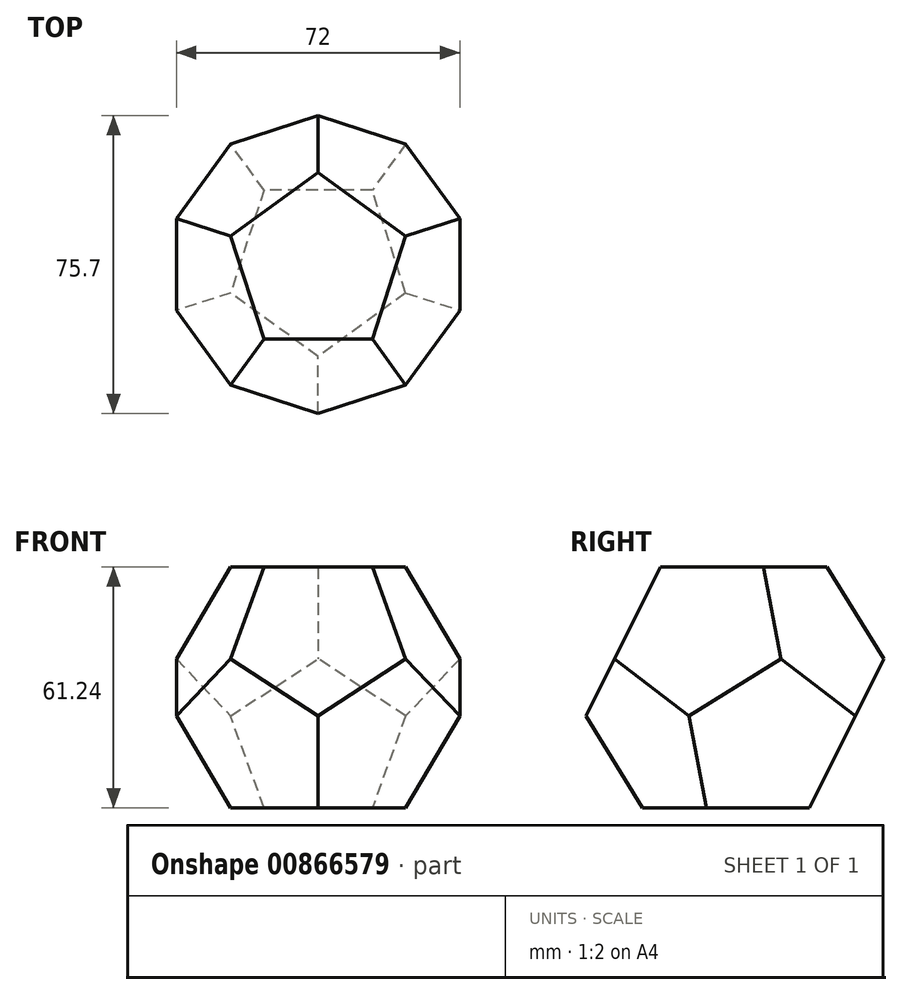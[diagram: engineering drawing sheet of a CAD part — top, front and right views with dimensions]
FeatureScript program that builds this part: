
annotation { "Feature Type Name" : "Feature", "Feature Type Description" : "" }
export const myFeature = defineFeature(function(context is Context, id is Id, definition is map)
    precondition{}
    {
        {
            var Q0;
            Q0=qCreatedBy(makeId("Top.planeOp"),FACE);
            var sketch = newSketch(context, id + "F0", { "sketchPlane" : qUnion([Q0])});
            skLineSegment(sketch, "E0.bottom", {"start": v(36, 36) * mm, "end": v(-36, 36) * mm, "construction": true});
            skLineSegment(sketch, "E0.top", {"start": v(36, -36) * mm, "end": v(-36, -36) * mm, "construction": true});
            skLineSegment(sketch, "E0.left", {"start": v(36, 36) * mm, "end": v(36, -36) * mm, "construction": true});
            skLineSegment(sketch, "E0.right", {"start": v(-36, 36) * mm, "end": v(-36, -36) * mm, "construction": true});
            skPoint(sketch, "E0.middle", {"position": v(0, 0) * mm});
            skCircle(sketch, "E1.cCircle", {"center": v(0, 0) * mm, "radius": 36 * mm, "construction": true});
            skLineSegment(sketch, "E1.0", {"start": v(-36, -11.7) * mm, "end": v(-36, 11.7) * mm});
            skLineSegment(sketch, "E1.1", {"start": v(-36, 11.7) * mm, "end": v(-22.25, 30.62) * mm});
            skLineSegment(sketch, "E1.2", {"start": v(-22.25, 30.62) * mm, "end": v(0, 37.85) * mm});
            skLineSegment(sketch, "E1.3", {"start": v(0, 37.85) * mm, "end": v(22.25, 30.62) * mm});
            skLineSegment(sketch, "E1.4", {"start": v(22.25, 30.62) * mm, "end": v(36, 11.7) * mm});
            skLineSegment(sketch, "E1.5", {"start": v(36, 11.7) * mm, "end": v(36, -11.7) * mm});
            skLineSegment(sketch, "E1.6", {"start": v(36, -11.7) * mm, "end": v(22.25, -30.62) * mm});
            skLineSegment(sketch, "E1.7", {"start": v(22.25, -30.62) * mm, "end": v(0, -37.85) * mm});
            skLineSegment(sketch, "E1.8", {"start": v(0, -37.85) * mm, "end": v(-22.25, -30.62) * mm});
            skLineSegment(sketch, "E1.9", {"start": v(-22.25, -30.62) * mm, "end": v(-36, -11.7) * mm});
            skPoint(sketch, "E1.0.midPoint", {"position": v(-36, 0) * mm});
            skSolve(sketch);
        }
        {
            var Q0;
            Q0 = qSketchRegion(id + "F0", true);
            extrude(context, id + "F1", {"entities" : qUnion([Q0]), "depth" : 61.25 * mm, "offsetDistance" : 25 * mm, "symmetric" : true});
        }
        {
            var Q0;
            Q0=makeQuery(id+"F1.opExtrude","CAP_FACE",FACE,{"disambiguationData":[OSD([sQuery(id+"F0.wireOp",EDGE,"E1.0"),sQuery(id+"F0.wireOp",EDGE,"E1.1"),sQuery(id+"F0.wireOp",EDGE,"E1.2"),sQuery(id+"F0.wireOp",EDGE,"E1.3"),sQuery(id+"F0.wireOp",EDGE,"E1.4"),sQuery(id+"F0.wireOp",EDGE,"E1.5"),sQuery(id+"F0.wireOp",EDGE,"E1.6"),sQuery(id+"F0.wireOp",EDGE,"E1.7"),sQuery(id+"F0.wireOp",EDGE,"E1.8"),sQuery(id+"F0.wireOp",EDGE,"E1.9")])],"isStart":false});
            var sketch = newSketch(context, id + "F2", { "sketchPlane" : qUnion([Q0])});
            skCircle(sketch, "E2.cCircle", {"center": v(0, 0) * mm, "radius": 23.4 * mm, "construction": true});
            skLineSegment(sketch, "E2.0", {"start": v(0, 23.4) * mm, "end": v(22.25, 7.23) * mm});
            skLineSegment(sketch, "E2.1", {"start": v(22.25, 7.23) * mm, "end": v(13.75, -18.93) * mm});
            skLineSegment(sketch, "E2.2", {"start": v(13.75, -18.93) * mm, "end": v(-13.75, -18.93) * mm});
            skLineSegment(sketch, "E2.3", {"start": v(-13.75, -18.93) * mm, "end": v(-22.25, 7.23) * mm});
            skLineSegment(sketch, "E2.4", {"start": v(-22.25, 7.23) * mm, "end": v(0, 23.4) * mm});
            skSolve(sketch);
        }
        {
            var Q0;
            Q0=qCreatedBy(makeId("Right.planeOp"),FACE);
            var sketch = newSketch(context, id + "F3", { "sketchPlane" : qUnion([Q0])});
            skPoint(sketch, "E3.0", {"position": v(-18.93, 30.62) * mm});
            skPoint(sketch, "E3.1", {"position": v(-37.85, 0) * mm});
            skPoint(sketch, "E4.0", {"position": v(-37.85, 30.62) * mm});
            skLineSegment(sketch, "E5", {"start": v(-18.93, 30.62) * mm, "end": v(-37.85, 30.62) * mm});
            skLineSegment(sketch, "E6", {"start": v(-18.93, 30.62) * mm, "end": v(-37.85, -7.23) * mm});
            skLineSegment(sketch, "E7", {"start": v(-37.85, -7.23) * mm, "end": v(-37.85, 30.62) * mm});
            skSolve(sketch);
        }
        {
            var Q0;
            Q0=makeQuery(id+"F2.imprint","IMPRINT",FACE,{"disambiguationData":[TD([[makeQuery(id+"F2.imprint","IMPRINT",EDGE,{"derivedFrom":sQuery(id+"F2.wireOp",EDGE,"E2.0")}),1.0]])]});
            var sketch = newSketch(context, id + "F4", { "sketchPlane" : qUnion([Q0])});
            skPoint(sketch, "E8.center", {"position": v(0, 0) * mm});
            skLineSegment(sketch, "E9.0.0", {"start": v(-36, -11.7) * mm, "end": v(-22.25, -30.62) * mm});
            skLineSegment(sketch, "E9.0.1", {"start": v(-22.25, -30.62) * mm, "end": v(0, -37.85) * mm});
            skLineSegment(sketch, "E9.0.2", {"start": v(0, -37.85) * mm, "end": v(22.25, -30.62) * mm});
            skLineSegment(sketch, "E9.0.3", {"start": v(22.25, -30.62) * mm, "end": v(36, -11.7) * mm});
            skLineSegment(sketch, "E9.0.4", {"start": v(36, -11.7) * mm, "end": v(36, 11.7) * mm});
            skLineSegment(sketch, "E9.0.5", {"start": v(36, 11.7) * mm, "end": v(22.25, 30.62) * mm});
            skLineSegment(sketch, "E9.0.6", {"start": v(22.25, 30.62) * mm, "end": v(0, 37.85) * mm});
            skLineSegment(sketch, "E9.0.7", {"start": v(0, 37.85) * mm, "end": v(-22.25, 30.62) * mm});
            skLineSegment(sketch, "E9.0.8", {"start": v(-22.25, 30.62) * mm, "end": v(-36, 11.7) * mm});
            skLineSegment(sketch, "E9.0.9", {"start": v(-36, 11.7) * mm, "end": v(-36, -11.7) * mm});
            skLineSegment(sketch, "E9.1", {"start": v(13.75, -18.93) * mm, "end": v(-13.75, -18.93) * mm});
            skLineSegment(sketch, "E9.2", {"start": v(-13.75, -18.93) * mm, "end": v(-22.25, 7.23) * mm});
            skLineSegment(sketch, "E9.3", {"start": v(-22.25, 7.23) * mm, "end": v(0, 23.4) * mm});
            skLineSegment(sketch, "E9.4", {"start": v(0, 23.4) * mm, "end": v(22.25, 7.23) * mm});
            skLineSegment(sketch, "E9.5", {"start": v(22.25, 7.23) * mm, "end": v(13.75, -18.93) * mm});
            skLineSegment(sketch, "E9.6", {"start": v(22.25, -30.62) * mm, "end": v(0, -37.85) * mm});
            skLineSegment(sketch, "E9.7", {"start": v(0, -37.85) * mm, "end": v(-22.25, -30.62) * mm});
            skLineSegment(sketch, "E9.8", {"start": v(-22.25, -30.62) * mm, "end": v(-36, -11.7) * mm});
            skLineSegment(sketch, "E9.9", {"start": v(-36, -11.7) * mm, "end": v(-36, 11.7) * mm});
            skLineSegment(sketch, "E9.10", {"start": v(-36, 11.7) * mm, "end": v(-22.25, 30.62) * mm});
            skLineSegment(sketch, "E9.11", {"start": v(-22.25, 30.62) * mm, "end": v(0, 37.85) * mm});
            skLineSegment(sketch, "E9.12", {"start": v(0, 37.85) * mm, "end": v(22.25, 30.62) * mm});
            skLineSegment(sketch, "E9.13", {"start": v(22.25, 30.62) * mm, "end": v(36, 11.7) * mm});
            skLineSegment(sketch, "E9.14", {"start": v(36, 11.7) * mm, "end": v(36, -11.7) * mm});
            skLineSegment(sketch, "E9.15", {"start": v(36, -11.7) * mm, "end": v(22.25, -30.62) * mm});
            skLineSegment(sketch, "E9.16.0", {"start": v(0, 23.4) * mm, "end": v(-22.25, 7.23) * mm});
            skLineSegment(sketch, "E9.16.1", {"start": v(-22.25, 7.23) * mm, "end": v(-13.75, -18.93) * mm});
            skLineSegment(sketch, "E9.16.2", {"start": v(-13.75, -18.93) * mm, "end": v(13.75, -18.93) * mm});
            skLineSegment(sketch, "E9.16.3", {"start": v(13.75, -18.93) * mm, "end": v(22.25, 7.23) * mm});
            skLineSegment(sketch, "E9.16.4", {"start": v(22.25, 7.23) * mm, "end": v(0, 23.4) * mm});
            skLineSegment(sketch, "E10", {"start": v(0, -18.93) * mm, "end": v(0, -37.85) * mm});
            skLineSegment(sketch, "E11", {"start": v(-18, -5.85) * mm, "end": v(-36, -11.7) * mm});
            skLineSegment(sketch, "E12", {"start": v(-22.25, 30.62) * mm, "end": v(-11.12, 15.31) * mm});
            skLineSegment(sketch, "E13", {"start": v(11.12, 15.31) * mm, "end": v(22.25, 30.62) * mm});
            skLineSegment(sketch, "E14", {"start": v(18, -5.85) * mm, "end": v(36, -11.7) * mm});
            skSolve(sketch);
        }
        {
            var Q0;
            Q0=sQuery(id+"F4.wireOp",EDGE,"E14");
            var Q1;
            Q1=makeQuery(id+"F1.opExtrude","SWEPT_EDGE",EDGE,{"disambiguationData":[OSD([sQuery(id+"F0.wireOp",EDGE,"E1.5"),sQuery(id+"F0.wireOp",EDGE,"E1.6")])]});
            cPlane(context, id + "F5", {"entities" : qUnion([Q0, Q1]), "cplaneType" : CPlaneType.LINE_ANGLE, "offset" : 0 * mm, "angle" : 0 * degree, "width" : 150 * mm, "height" : 150 * mm});
        }
        {
            var Q0;
            Q0=qCreatedBy(id+"F5.planeOp",FACE);
            var sketch = newSketch(context, id + "F6", { "sketchPlane" : qUnion([Q0])});
            skLineSegment(sketch, "E15.0", {"start": v(-18.93, 30.62) * mm, "end": v(-37.85, 30.62) * mm});
            skPoint(sketch, "E15.1", {"position": v(-37.85, 0) * mm});
            skLineSegment(sketch, "E16", {"start": v(-18.93, 30.62) * mm, "end": v(-37.85, -7.23) * mm});
            skLineSegment(sketch, "E17", {"start": v(-37.85, -7.23) * mm, "end": v(-37.85, 30.62) * mm});
            skSolve(sketch);
        }
        {
            var Q0;
            Q0=makeQuery(id+"F1.opExtrude","SWEPT_EDGE",EDGE,{"disambiguationData":[OSD([sQuery(id+"F0.wireOp",EDGE,"E1.3"),sQuery(id+"F0.wireOp",EDGE,"E1.4")])]});
            var Q1;
            Q1=sQuery(id+"F4.wireOp",EDGE,"E13");
            cPlane(context, id + "F7", {"entities" : qUnion([Q0, Q1]), "cplaneType" : CPlaneType.LINE_ANGLE, "offset" : 25 * mm, "angle" : 0 * degree, "width" : 150 * mm, "height" : 150 * mm});
        }
        {
            var Q0;
            Q0=qCreatedBy(id+"F7.planeOp",FACE);
            var sketch = newSketch(context, id + "F8", { "sketchPlane" : qUnion([Q0])});
            skLineSegment(sketch, "E18.0", {"start": v(37.85, 30.62) * mm, "end": v(18.93, 30.62) * mm});
            skPoint(sketch, "E18.1", {"position": v(37.85, 0) * mm});
            skLineSegment(sketch, "E19", {"start": v(18.93, 30.62) * mm, "end": v(37.85, -7.23) * mm});
            skLineSegment(sketch, "E20", {"start": v(37.85, -7.23) * mm, "end": v(37.85, 30.62) * mm});
            skSolve(sketch);
        }
        {
            var Q0;
            Q0=makeQuery(id+"F1.opExtrude","SWEPT_EDGE",EDGE,{"disambiguationData":[OSD([sQuery(id+"F0.wireOp",EDGE,"E1.1"),sQuery(id+"F0.wireOp",EDGE,"E1.2")])]});
            var Q1;
            Q1=sQuery(id+"F4.wireOp",EDGE,"E12");
            cPlane(context, id + "F9", {"entities" : qUnion([Q0, Q1]), "cplaneType" : CPlaneType.LINE_ANGLE, "offset" : 25 * mm, "angle" : 0 * degree, "width" : 150 * mm, "height" : 150 * mm});
        }
        {
            var Q0;
            Q0=qCreatedBy(id+"F9.planeOp",FACE);
            var sketch = newSketch(context, id + "F10", { "sketchPlane" : qUnion([Q0])});
            skPoint(sketch, "E21.1", {"position": v(-37.85, 0) * mm});
            skLineSegment(sketch, "E22.0", {"start": v(-37.85, 30.62) * mm, "end": v(-18.93, 30.62) * mm});
            skLineSegment(sketch, "E23", {"start": v(-18.93, 30.62) * mm, "end": v(-37.85, -7.23) * mm});
            skLineSegment(sketch, "E24", {"start": v(-37.85, -7.23) * mm, "end": v(-37.85, 30.62) * mm});
            skSolve(sketch);
        }
        {
            var Q0;
            Q0=makeQuery(id+"F1.opExtrude","SWEPT_EDGE",EDGE,{"disambiguationData":[OSD([sQuery(id+"F0.wireOp",EDGE,"E1.0"),sQuery(id+"F0.wireOp",EDGE,"E1.9")])]});
            var Q1;
            Q1=sQuery(id+"F4.wireOp",EDGE,"E11");
            cPlane(context, id + "F11", {"entities" : qUnion([Q0, Q1]), "cplaneType" : CPlaneType.LINE_ANGLE, "offset" : 25 * mm, "angle" : 0 * degree, "width" : 150 * mm, "height" : 150 * mm});
        }
        {
            var Q0;
            Q0=qCreatedBy(id+"F11.planeOp",FACE);
            var sketch = newSketch(context, id + "F12", { "sketchPlane" : qUnion([Q0])});
            skLineSegment(sketch, "E25.1", {"start": v(37.85, 30.62) * mm, "end": v(37.85, -30.62) * mm});
            skPoint(sketch, "E25.2", {"position": v(37.85, 0) * mm});
            skLineSegment(sketch, "E26", {"start": v(18.93, 30.62) * mm, "end": v(37.85, -7.23) * mm});
            skLineSegment(sketch, "E27", {"start": v(37.85, -7.23) * mm, "end": v(37.85, 26.07) * mm});
            skPoint(sketch, "E28.0", {"position": v(18.93, 30.62) * mm});
            skLineSegment(sketch, "E29.0", {"start": v(18.93, 30.62) * mm, "end": v(37.85, 30.62) * mm});
            skSolve(sketch);
        }
        {
            var Q0;
            Q0 = qSketchRegion(id + "F3", true);
            extrude(context, id + "F13", {"entities" : qUnion([Q0]), "operationType" : NewBodyOperationType.REMOVE, "depth" : 100 * mm, "offsetDistance" : 25 * mm, "symmetric" : true});
        }
        {
            var Q0;
            Q0 = qSketchRegion(id + "F6", true);
            extrude(context, id + "F14", {"entities" : qUnion([Q0]), "operationType" : NewBodyOperationType.REMOVE, "oppositeDirection" : true, "depth" : 1000 * mm, "offsetDistance" : 25 * mm, "symmetric" : true});
        }
        {
            var Q0;
            Q0 = qSketchRegion(id + "F8", true);
            extrude(context, id + "F15", {"entities" : qUnion([Q0]), "operationType" : NewBodyOperationType.REMOVE, "oppositeDirection" : true, "depth" : 1000 * mm, "offsetDistance" : 25 * mm, "symmetric" : true});
        }
        {
            var Q0;
            Q0 = qSketchRegion(id + "F10", true);
            extrude(context, id + "F16", {"entities" : qUnion([Q0]), "operationType" : NewBodyOperationType.REMOVE, "oppositeDirection" : true, "depth" : 1000 * mm, "offsetDistance" : 25 * mm, "symmetric" : true});
        }
        {
            var Q0;
            Q0 = qSketchRegion(id + "F12", true);
            extrude(context, id + "F17", {"entities" : qUnion([Q0]), "operationType" : NewBodyOperationType.REMOVE, "oppositeDirection" : true, "depth" : 1000 * mm, "offsetDistance" : 25 * mm, "symmetric" : true});
        }
        {
            var Q0;
            Q0=makeQuery(id+"F1.opExtrude","CAP_FACE",FACE,{"disambiguationData":[OSD([sQuery(id+"F0.wireOp",EDGE,"E1.0"),sQuery(id+"F0.wireOp",EDGE,"E1.1"),sQuery(id+"F0.wireOp",EDGE,"E1.2"),sQuery(id+"F0.wireOp",EDGE,"E1.3"),sQuery(id+"F0.wireOp",EDGE,"E1.4"),sQuery(id+"F0.wireOp",EDGE,"E1.5"),sQuery(id+"F0.wireOp",EDGE,"E1.6"),sQuery(id+"F0.wireOp",EDGE,"E1.7"),sQuery(id+"F0.wireOp",EDGE,"E1.8"),sQuery(id+"F0.wireOp",EDGE,"E1.9")])],"isStart":true});
            var sketch = newSketch(context, id + "F18", { "sketchPlane" : qUnion([Q0])});
            skCircle(sketch, "E30.cCircle", {"center": v(0, 0) * mm, "radius": 23.4 * mm, "construction": true});
            skLineSegment(sketch, "E30.0", {"start": v(0, 23.4) * mm, "end": v(22.25, 7.23) * mm});
            skLineSegment(sketch, "E30.1", {"start": v(22.25, 7.23) * mm, "end": v(13.75, -18.93) * mm});
            skLineSegment(sketch, "E30.2", {"start": v(13.75, -18.93) * mm, "end": v(-13.75, -18.93) * mm});
            skLineSegment(sketch, "E30.3", {"start": v(-13.75, -18.93) * mm, "end": v(-22.25, 7.23) * mm});
            skLineSegment(sketch, "E30.4", {"start": v(-22.25, 7.23) * mm, "end": v(0, 23.4) * mm});
            skLineSegment(sketch, "E31", {"start": v(11.12, 15.31) * mm, "end": v(22.25, 30.62) * mm});
            skLineSegment(sketch, "E32", {"start": v(-11.12, 15.31) * mm, "end": v(-22.25, 30.62) * mm});
            skLineSegment(sketch, "E33", {"start": v(-18, -5.85) * mm, "end": v(-36, -11.7) * mm});
            skLineSegment(sketch, "E34", {"start": v(0, -18.93) * mm, "end": v(0, -37.85) * mm});
            skLineSegment(sketch, "E35", {"start": v(18, -5.85) * mm, "end": v(36, -11.7) * mm});
            skSolve(sketch);
        }
        {
            var Q0;
            Q0=qCreatedBy(makeId("Right.planeOp"),FACE);
            var sketch = newSketch(context, id + "F19", { "sketchPlane" : qUnion([Q0])});
            skLineSegment(sketch, "E36.0", {"start": v(18.93, -30.62) * mm, "end": v(37.85, -30.62) * mm});
            skLineSegment(sketch, "E37.0", {"start": v(37.85, 7.23) * mm, "end": v(37.85, -30.62) * mm});
            skLineSegment(sketch, "E38", {"start": v(18.93, -30.62) * mm, "end": v(37.85, 7.23) * mm});
            skSolve(sketch);
        }
        {
            var Q0;
            Q0=qCreatedBy(id+"F11.planeOp",FACE);
            var sketch = newSketch(context, id + "F20", { "sketchPlane" : qUnion([Q0])});
            skLineSegment(sketch, "E39.0", {"start": v(-18.93, -30.62) * mm, "end": v(-37.85, -30.62) * mm});
            skLineSegment(sketch, "E39.1", {"start": v(-37.85, 7.23) * mm, "end": v(-37.85, -30.62) * mm});
            skLineSegment(sketch, "E40", {"start": v(-18.93, -30.62) * mm, "end": v(-37.85, 7.23) * mm});
            skSolve(sketch);
        }
        {
            var Q0;
            Q0=qCreatedBy(id+"F9.planeOp",FACE);
            var sketch = newSketch(context, id + "F21", { "sketchPlane" : qUnion([Q0])});
            skLineSegment(sketch, "E41.0", {"start": v(18.93, -30.62) * mm, "end": v(37.85, -30.62) * mm});
            skLineSegment(sketch, "E41.1", {"start": v(37.85, 7.23) * mm, "end": v(37.85, -30.62) * mm});
            skLineSegment(sketch, "E42", {"start": v(18.93, -30.62) * mm, "end": v(37.85, 7.23) * mm});
            skSolve(sketch);
        }
        {
            var Q0;
            Q0=qCreatedBy(id+"F7.planeOp",FACE);
            var sketch = newSketch(context, id + "F22", { "sketchPlane" : qUnion([Q0])});
            skLineSegment(sketch, "E43.0", {"start": v(-18.93, -30.62) * mm, "end": v(-37.85, -30.62) * mm});
            skLineSegment(sketch, "E43.1", {"start": v(-37.85, 7.23) * mm, "end": v(-37.85, -30.62) * mm});
            skLineSegment(sketch, "E44", {"start": v(-18.93, -30.62) * mm, "end": v(-37.85, 7.23) * mm});
            skSolve(sketch);
        }
        {
            var Q0;
            Q0=qCreatedBy(id+"F5.planeOp",FACE);
            var sketch = newSketch(context, id + "F23", { "sketchPlane" : qUnion([Q0])});
            skLineSegment(sketch, "E45.0", {"start": v(18.93, -30.62) * mm, "end": v(37.85, -30.62) * mm});
            skLineSegment(sketch, "E45.1", {"start": v(37.85, 7.23) * mm, "end": v(37.85, -30.62) * mm});
            skLineSegment(sketch, "E46", {"start": v(18.93, -30.62) * mm, "end": v(37.85, 7.23) * mm});
            skSolve(sketch);
        }
        {
            var Q0;
            Q0 = qSketchRegion(id + "F19", true);
            extrude(context, id + "F24", {"entities" : qUnion([Q0]), "operationType" : NewBodyOperationType.REMOVE, "depth" : 1000 * mm, "offsetDistance" : 25 * mm, "symmetric" : true});
        }
        {
            var Q0;
            Q0 = qSketchRegion(id + "F20", true);
            extrude(context, id + "F25", {"entities" : qUnion([Q0]), "operationType" : NewBodyOperationType.REMOVE, "oppositeDirection" : true, "depth" : 1000 * mm, "offsetDistance" : 25 * mm, "symmetric" : true});
        }
        {
            var Q0;
            Q0 = qSketchRegion(id + "F21", true);
            extrude(context, id + "F26", {"entities" : qUnion([Q0]), "operationType" : NewBodyOperationType.REMOVE, "oppositeDirection" : true, "depth" : 1000 * mm, "offsetDistance" : 25 * mm, "symmetric" : true});
        }
        {
            var Q0;
            Q0 = qSketchRegion(id + "F22", true);
            extrude(context, id + "F27", {"entities" : qUnion([Q0]), "operationType" : NewBodyOperationType.REMOVE, "depth" : 1000 * mm, "offsetDistance" : 25 * mm, "symmetric" : true});
        }
        {
            var Q0;
            Q0 = qSketchRegion(id + "F23", true);
            extrude(context, id + "F28", {"entities" : qUnion([Q0]), "operationType" : NewBodyOperationType.REMOVE, "depth" : 1000 * mm, "offsetDistance" : 25 * mm, "symmetric" : true});
        }
    });
